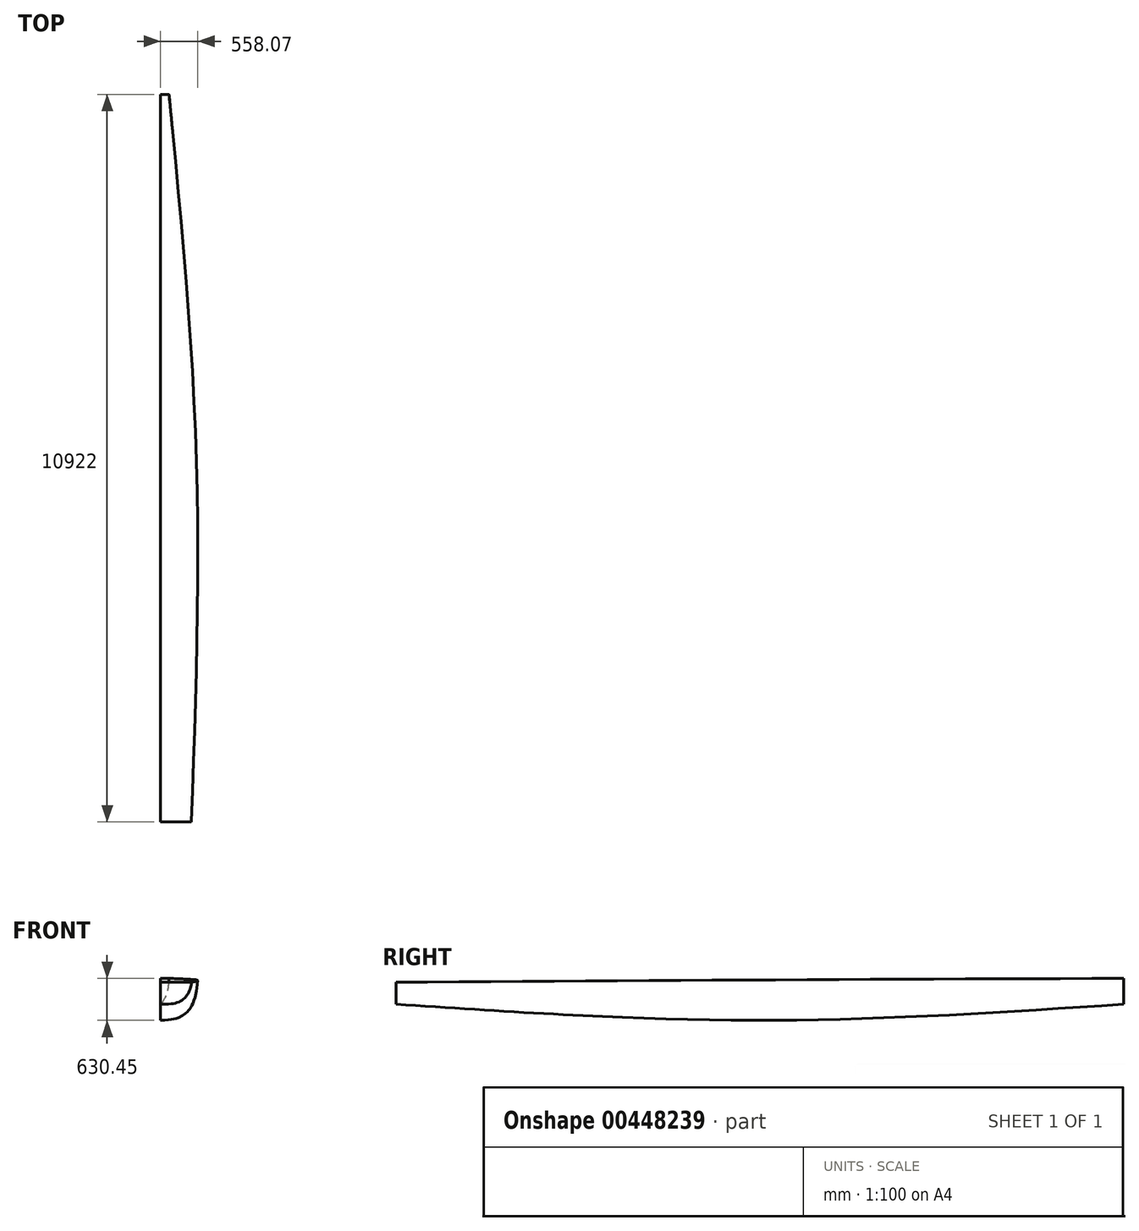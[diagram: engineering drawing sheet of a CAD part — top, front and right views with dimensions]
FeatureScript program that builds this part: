
annotation { "Feature Type Name" : "Feature", "Feature Type Description" : "" }
export const myFeature = defineFeature(function(context is Context, id is Id, definition is map)
    precondition{}
    {
        {
            var Q0;
            Q0=qCreatedBy(makeId("Front.planeOp"),FACE);
            cPlane(context, id + "F0", {"entities" : qUnion([Q0]), "cplaneType" : CPlaneType.OFFSET, "offset" : 5461 * mm, "width" : 152.4 * mm, "height" : 152.4 * mm});
        }
        {
            var Q0;
            Q0=qCreatedBy(makeId("Front.planeOp"),FACE);
            cPlane(context, id + "F1", {"entities" : qUnion([Q0]), "cplaneType" : CPlaneType.OFFSET, "offset" : 10922 * mm, "width" : 152.4 * mm, "height" : 152.4 * mm});
        }
        {
            var Q0;
            Q0=qCreatedBy(makeId("Front.planeOp"),FACE);
            var sketch = newSketch(context, id + "F2", { "sketchPlane" : qUnion([Q0])});
            skFitSpline(sketch, "E0", {"points": [v(0, 0) * mm, v(96.25, 169.66) * mm, v(126.84, 388.02) * mm], "startDerivative": vector(237.02, 203.16) * mm, "endDerivative": vector(-18.28, 339.3) * mm});
            skLineSegment(sketch, "E1", {"start": v(126.84, 388.02) * mm, "end": v(0, 388.02) * mm});
            skLineSegment(sketch, "E2", {"start": v(0, 388.02) * mm, "end": v(0, 0) * mm});
            skSolve(sketch);
        }
        {
            var Q0;
            Q0=qCreatedBy(id+"F0.planeOp",FACE);
            var sketch = newSketch(context, id + "F3", { "sketchPlane" : qUnion([Q0])});
            skFitSpline(sketch, "E3", {"points": [v(0, -242.43) * mm, v(431.54, -57.3) * mm, v(536.58, 364.97) * mm], "startDerivative": vector(1680.92, 34.88) * mm, "endDerivative": vector(103.59, 1370.35) * mm});
            skLineSegment(sketch, "E4", {"start": v(0, -242.43) * mm, "end": v(0, 364.97) * mm});
            skLineSegment(sketch, "E5", {"start": v(0, 364.97) * mm, "end": v(536.58, 364.97) * mm});
            skSolve(sketch);
        }
        {
            var Q0;
            Q0=qCreatedBy(id+"F1.planeOp",FACE);
            var sketch = newSketch(context, id + "F4", { "sketchPlane" : qUnion([Q0])});
            skFitSpline(sketch, "E6", {"points": [v(0, 0) * mm, v(377.2, 110.1) * mm, v(463.84, 328.88) * mm], "startDerivative": vector(1024, -31.85) * mm, "endDerivative": vector(-0.4, 370.21) * mm});
            skLineSegment(sketch, "E7", {"start": v(463.84, 328.88) * mm, "end": v(0, 328.88) * mm});
            skLineSegment(sketch, "E8", {"start": v(0, 328.88) * mm, "end": v(0, 0) * mm});
            skSolve(sketch);
        }
        {
            var Q0;
            Q0=makeQuery(id+"F4.imprint","IMPRINT",FACE,{"disambiguationData":[TD([[makeQuery(id+"F4.imprint","IMPRINT",EDGE,{"derivedFrom":sQuery(id+"F4.wireOp",EDGE,"E6")}),1.0]])]});
            var Q1;
            Q1=makeQuery(id+"F3.imprint","IMPRINT",FACE,{"disambiguationData":[TD([[makeQuery(id+"F3.imprint","IMPRINT",EDGE,{"derivedFrom":sQuery(id+"F3.wireOp",EDGE,"E3")}),1.0]])]});
            var Q2;
            Q2=makeQuery(id+"F2.imprint","IMPRINT",FACE,{"disambiguationData":[TD([[makeQuery(id+"F2.imprint","IMPRINT",EDGE,{"derivedFrom":sQuery(id+"F2.wireOp",EDGE,"E0")}),1.0]])]});
            loft(context, id + "F5", {"sheetProfilesArray" : [{ "sheetProfileEntities" : qUnion([Q0]) }, { "sheetProfileEntities" : qUnion([Q1]) }, { "sheetProfileEntities" : qUnion([Q2]) }]});
        }
    });
